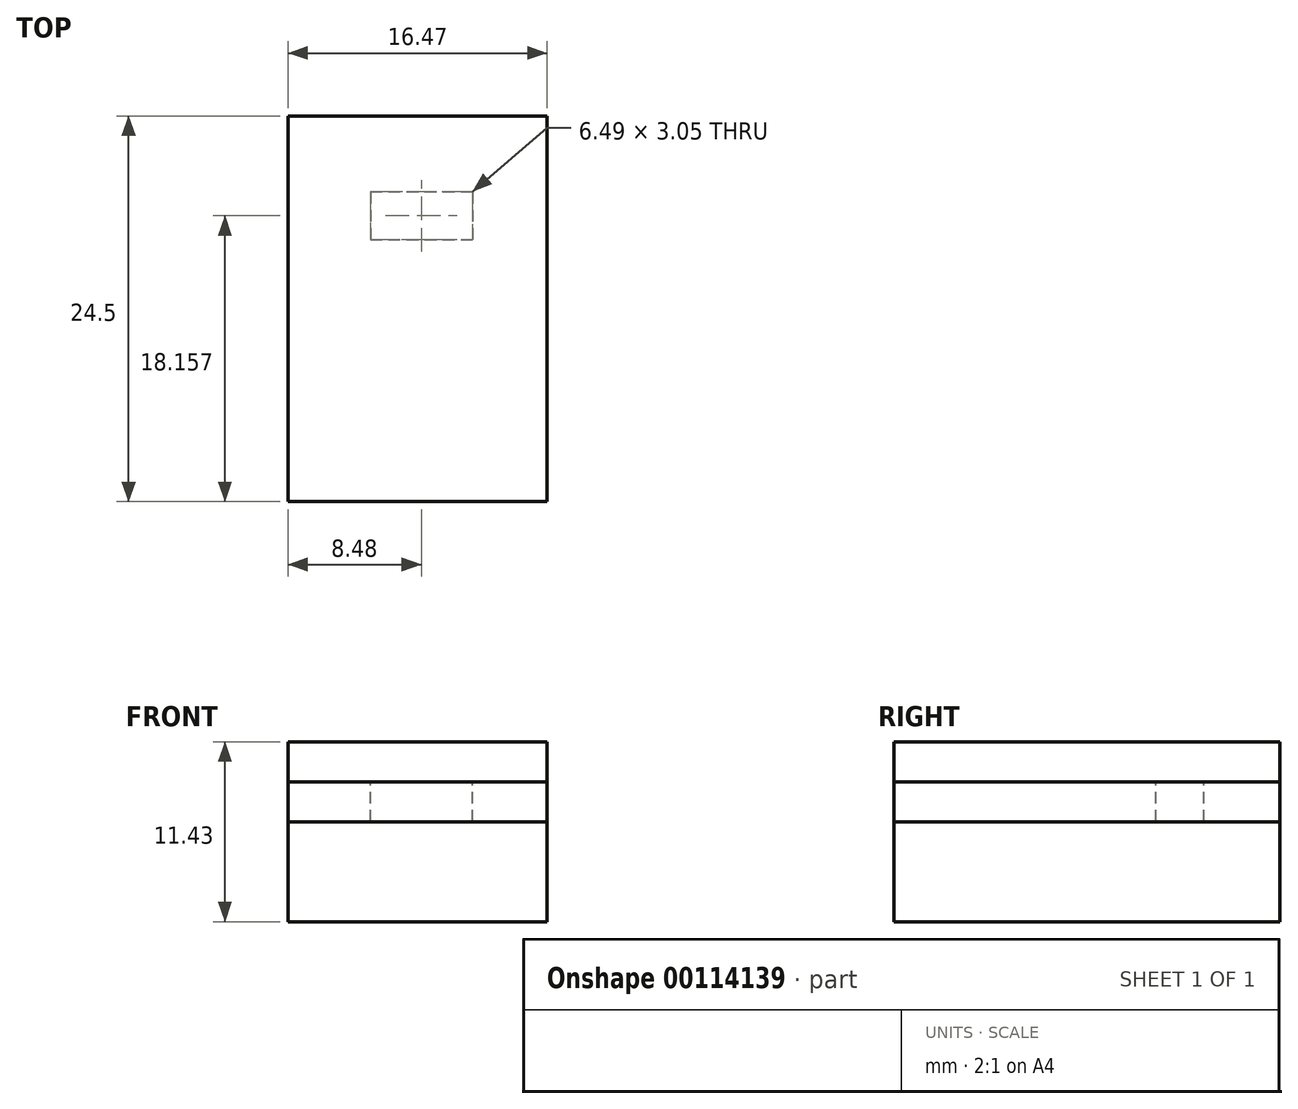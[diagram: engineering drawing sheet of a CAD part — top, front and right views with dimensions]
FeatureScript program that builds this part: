
annotation { "Feature Type Name" : "Feature", "Feature Type Description" : "" }
export const myFeature = defineFeature(function(context is Context, id is Id, definition is map)
    precondition{}
    {
        {
            var Q0;
            Q0=qCreatedBy(makeId("Top.planeOp"),FACE);
            var sketch = newSketch(context, id + "F0", { "sketchPlane" : qUnion([Q0])});
            skLineSegment(sketch, "E0.bottom", {"start": v(-7.99, 12.48) * mm, "end": v(8.48, 12.48) * mm});
            skLineSegment(sketch, "E0.top", {"start": v(-7.99, -12.02) * mm, "end": v(8.48, -12.02) * mm});
            skLineSegment(sketch, "E0.left", {"start": v(-7.99, 12.48) * mm, "end": v(-7.99, -12.02) * mm});
            skLineSegment(sketch, "E0.right", {"start": v(8.48, 12.48) * mm, "end": v(8.48, -12.02) * mm});
            skSolve(sketch);
        }
        {
            var Q0;
            Q0=makeQuery(id+"F0.imprint","IMPRINT",FACE,{"disambiguationData":[TD([[makeQuery(id+"F0.imprint","IMPRINT",EDGE,{"derivedFrom":sQuery(id+"F0.wireOp",EDGE,"E0.bottom")}),-1.0]])]});
            extrude(context, id + "F1", {"entities" : qUnion([Q0]), "depth" : 6.35 * mm});
        }
        {
            var Q0;
            Q0=makeQuery(id+"F1.opExtrude","CAP_FACE",FACE,{"disambiguationData":[OSD([sQuery(id+"F0.wireOp",EDGE,"E0.bottom"),sQuery(id+"F0.wireOp",EDGE,"E0.top"),sQuery(id+"F0.wireOp",EDGE,"E0.left"),sQuery(id+"F0.wireOp",EDGE,"E0.right")])],"isStart":false});
            var sketch = newSketch(context, id + "F2", { "sketchPlane" : qUnion([Q0])});
            skLineSegment(sketch, "E1.bottom", {"start": v(-7.99, 12.48) * mm, "end": v(8.48, 12.48) * mm});
            skLineSegment(sketch, "E1.top", {"start": v(-7.99, -12.02) * mm, "end": v(8.48, -12.02) * mm});
            skLineSegment(sketch, "E1.left", {"start": v(-7.99, 12.48) * mm, "end": v(-7.99, -12.02) * mm});
            skLineSegment(sketch, "E1.right", {"start": v(8.48, 12.48) * mm, "end": v(8.48, -12.02) * mm});
            skSolve(sketch);
        }
        {
            var Q0;
            Q0=qSketchRegion(id+"F2",true);
            var Q1;
            Q1=qSketchRegion(id+"F4",true);
            extrude(context, id + "F3", {"entities" : qUnion([Q0, Q1]), "depth" : 2.54 * mm});
        }
        {
            var Q0;
            Q0=makeQuery(id+"F3.opExtrude","CAP_FACE",FACE,{"disambiguationData":[OSD([sQuery(id+"F2.wireOp",EDGE,"E1.bottom"),sQuery(id+"F2.wireOp",EDGE,"E1.top"),sQuery(id+"F2.wireOp",EDGE,"E1.left"),sQuery(id+"F2.wireOp",EDGE,"E1.right")])],"isStart":false});
            var sketch = newSketch(context, id + "F4", { "sketchPlane" : qUnion([Q0])});
            skLineSegment(sketch, "E2.bottom", {"start": v(-2.76, 7.66) * mm, "end": v(3.74, 7.66) * mm});
            skLineSegment(sketch, "E2.top", {"start": v(-2.76, 4.61) * mm, "end": v(3.74, 4.61) * mm});
            skLineSegment(sketch, "E2.left", {"start": v(-2.76, 7.66) * mm, "end": v(-2.76, 4.61) * mm});
            skLineSegment(sketch, "E2.right", {"start": v(3.74, 7.66) * mm, "end": v(3.74, 4.61) * mm});
            skSolve(sketch);
        }
        {
            var Q0;
            Q0=qSketchRegion(id+"F4",true);
            extrude(context, id + "F5", {"entities" : qUnion([Q0]), "operationType" : NewBodyOperationType.REMOVE, "oppositeDirection" : true, "depth" : 2.54 * mm});
        }
        {
            var Q0;
            Q0=makeQuery(id+"F3.opExtrude","CAP_FACE",FACE,{"disambiguationData":[OSD([sQuery(id+"F2.wireOp",EDGE,"E1.bottom"),sQuery(id+"F2.wireOp",EDGE,"E1.top"),sQuery(id+"F2.wireOp",EDGE,"E1.left"),sQuery(id+"F2.wireOp",EDGE,"E1.right")])],"isStart":false});
            var sketch = newSketch(context, id + "F6", { "sketchPlane" : qUnion([Q0])});
            skLineSegment(sketch, "E3.bottom", {"start": v(-7.99, 12.48) * mm, "end": v(8.48, 12.48) * mm});
            skLineSegment(sketch, "E3.top", {"start": v(-7.99, -12.02) * mm, "end": v(8.48, -12.02) * mm});
            skLineSegment(sketch, "E3.left", {"start": v(-7.99, 12.48) * mm, "end": v(-7.99, -12.02) * mm});
            skLineSegment(sketch, "E3.right", {"start": v(8.48, 12.48) * mm, "end": v(8.48, -12.02) * mm});
            skSolve(sketch);
        }
        {
            var Q0;
            Q0 = qSketchRegion(id + "F6", true);
            extrude(context, id + "F7", {"entities" : qUnion([Q0]), "depth" : 2.54 * mm});
        }
    });
